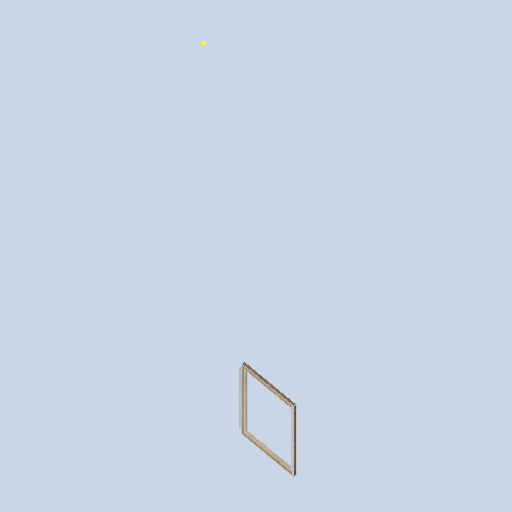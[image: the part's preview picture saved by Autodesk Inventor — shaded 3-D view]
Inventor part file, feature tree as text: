
AUTODESK INVENTOR PART (.ipt)
format: ipt  version: 2024.2 (Build 282272000, 272)  size: 124,928 bytes
history: native  units: in
note: dims shown in document units (in); Inventor stores cm internally (conversion verified against a paired STEP export)
features: sketch x9, plane x4, other x3
ambient origin geometry x8: Origin, YZ Plane, XZ Plane, XY Plane, X Axis, Y Axis, Z Axis, Center Point
bodies: Solid1 (feature_tree)
feature tree (16):
  other  "eave_frame_side.ipt"
  other  "Solid1::eave_frame_side.ipt"
  other  "TaggingFeature1"
  sketch  "Sketch1"  dims[d0=0.3937in]
  sketch  "Sketch2"
  sketch  "Sketch3"
  sketch  "Sketch4"
  sketch  "Sketch5"
  sketch  "Sketch6"
  sketch  "Sketch7"
  sketch  "Sketch8"
  sketch  "Sketch9"
  plane  "Work Plane1"
  plane  "Work Plane2"
  plane  "Work Plane3"
  plane  "Work Plane4"
